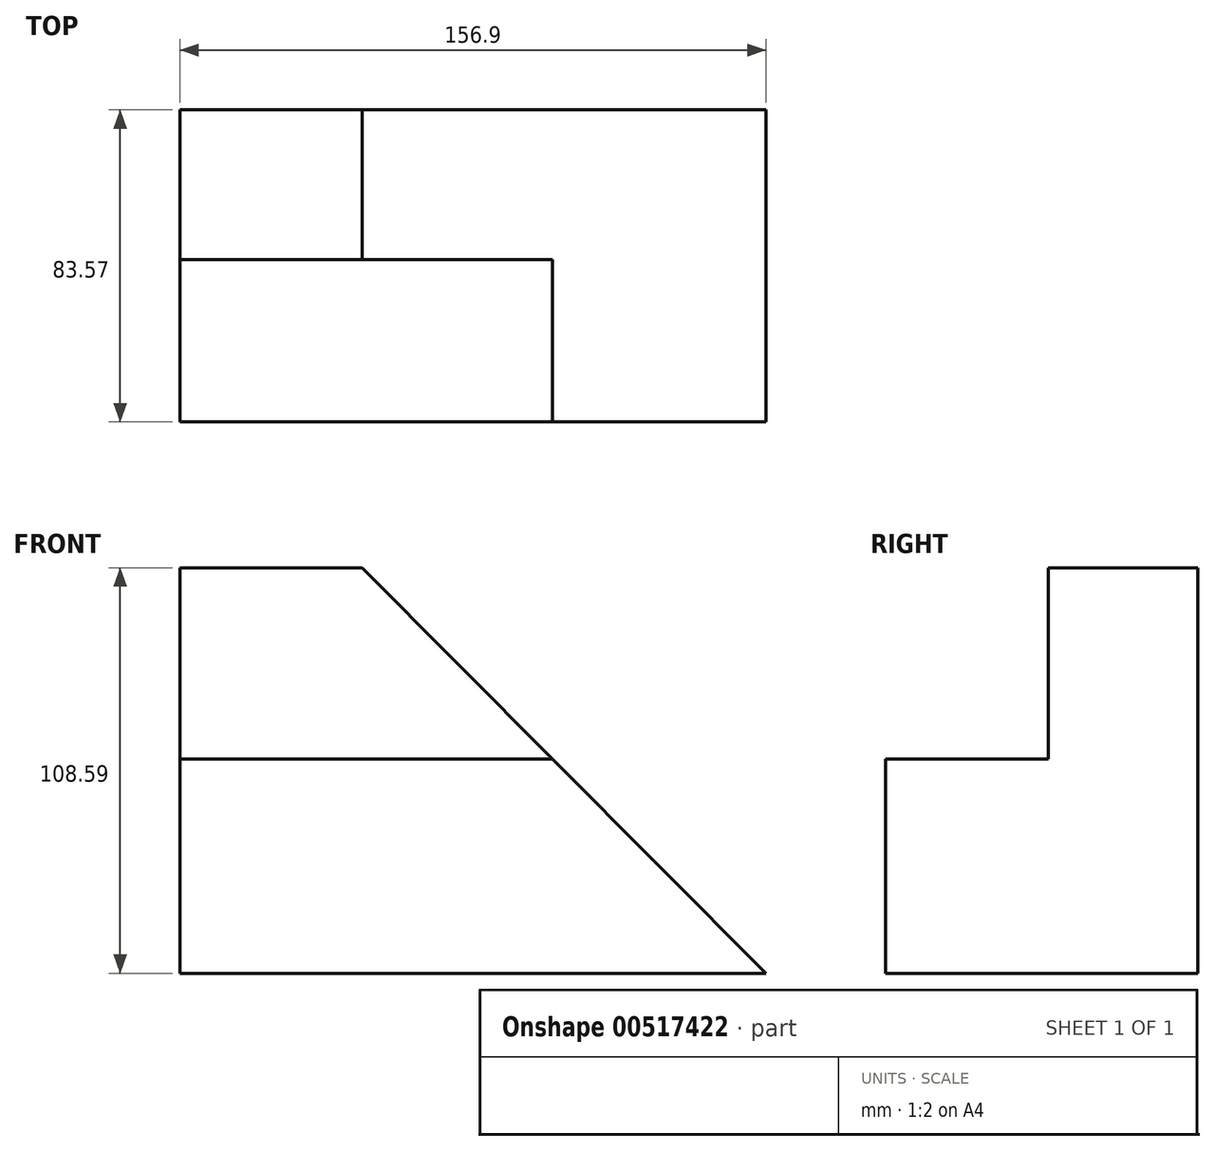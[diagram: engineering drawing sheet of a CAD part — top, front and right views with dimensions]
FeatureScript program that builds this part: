
annotation { "Feature Type Name" : "Feature", "Feature Type Description" : "" }
export const myFeature = defineFeature(function(context is Context, id is Id, definition is map)
    precondition{}
    {
        {
            var Q0;
            Q0=qCreatedBy(makeId("Front.planeOp"),FACE);
            var sketch = newSketch(context, id + "F0", { "sketchPlane" : qUnion([Q0])});
            skLineSegment(sketch, "E0.bottom", {"start": v(-62.5, 31.53) * mm, "end": v(94.4, 31.53) * mm});
            skLineSegment(sketch, "E0.top", {"start": v(-62.5, -77.06) * mm, "end": v(94.4, -77.06) * mm});
            skLineSegment(sketch, "E0.left", {"start": v(-62.5, 31.53) * mm, "end": v(-62.5, -77.06) * mm});
            skLineSegment(sketch, "E0.right", {"start": v(94.4, 31.53) * mm, "end": v(94.4, -77.06) * mm});
            skSolve(sketch);
        }
        {
            var Q0;
            Q0 = qSketchRegion(id + "F0", true);
            extrude(context, id + "F1", {"entities" : qUnion([Q0]), "depth" : 83.57 * mm, "offsetDistance" : 25.4 * mm});
        }
        {
            var Q0;
            Q0=makeQuery(id+"F1.opExtrude","CAP_FACE",FACE,{"disambiguationData":[OSD([sQuery(id+"F0.wireOp",EDGE,"E0.bottom"),sQuery(id+"F0.wireOp",EDGE,"E0.top"),sQuery(id+"F0.wireOp",EDGE,"E0.left"),sQuery(id+"F0.wireOp",EDGE,"E0.right")])],"isStart":false});
            var sketch = newSketch(context, id + "F2", { "sketchPlane" : qUnion([Q0])});
            skLineSegment(sketch, "E1", {"start": v(-13.76, 31.53) * mm, "end": v(94.4, -77.06) * mm});
            skSolve(sketch);
        }
        {
            var Q0;
            {var subQ0=sQuery(id+"F2.wireOp",EDGE,"E1");Q0=makeQuery(id+"F2.imprint","IMPRINT",FACE,{"disambiguationData":[TD([[makeQuery(id+"F2.imprint","IMPRINT",EDGE,{"derivedFrom":subQ0}),1.0]])]});}
            extrude(context, id + "F3", {"entities" : qUnion([Q0]), "operationType" : NewBodyOperationType.REMOVE, "endBound" : BoundingType.THROUGH_ALL, "oppositeDirection" : true, "depth" : 25.4 * mm, "offsetDistance" : 25.4 * mm});
        }
        {
            var Q0;
            Q0=makeQuery(id+"F1.opExtrude","SWEPT_FACE",FACE,{"disambiguationData":[OSD([sQuery(id+"F0.wireOp",EDGE,"E0.left")])]});
            var sketch = newSketch(context, id + "F4", { "sketchPlane" : qUnion([Q0])});
            skLineSegment(sketch, "E2.bottom", {"start": v(40.07, 31.53) * mm, "end": v(83.57, 31.53) * mm});
            skLineSegment(sketch, "E2.top", {"start": v(40.07, -19.68) * mm, "end": v(83.57, -19.68) * mm});
            skLineSegment(sketch, "E2.left", {"start": v(40.07, 31.53) * mm, "end": v(40.07, -19.68) * mm});
            skLineSegment(sketch, "E2.right", {"start": v(83.57, 31.53) * mm, "end": v(83.57, -19.68) * mm});
            skSolve(sketch);
        }
        {
            var Q0;
            Q0 = qSketchRegion(id + "F4", true);
            extrude(context, id + "F5", {"entities" : qUnion([Q0]), "operationType" : NewBodyOperationType.REMOVE, "endBound" : BoundingType.THROUGH_ALL, "oppositeDirection" : true, "depth" : 25.4 * mm, "offsetDistance" : 25.4 * mm});
        }
    });
